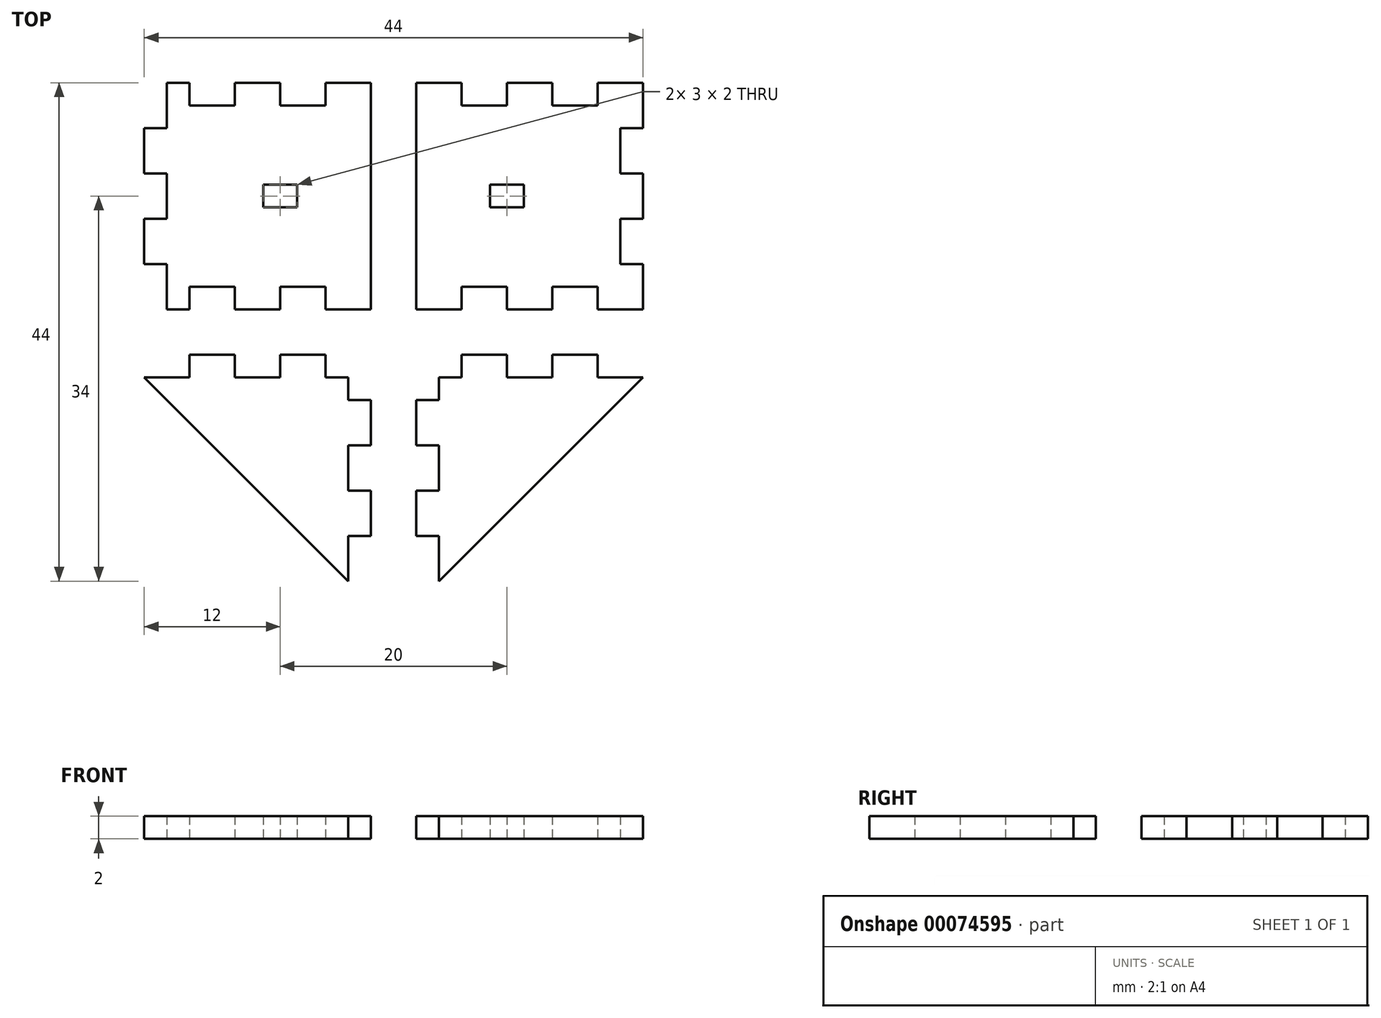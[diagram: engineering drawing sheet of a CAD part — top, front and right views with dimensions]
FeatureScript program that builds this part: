
annotation { "Feature Type Name" : "Feature", "Feature Type Description" : "" }
export const myFeature = defineFeature(function(context is Context, id is Id, definition is map)
    precondition{}
    {
        {
            var Q0;
            Q0=qCreatedBy(makeId("Top.planeOp"),FACE);
            var sketch = newSketch(context, id + "F3", { "sketchPlane" : qUnion([Q0])});
            skLineSegment(sketch, "E0", {"start": v(2, 0) * mm, "end": v(6, 0) * mm});
            skLineSegment(sketch, "E1", {"start": v(6, 0) * mm, "end": v(6, 2) * mm});
            skLineSegment(sketch, "E2", {"start": v(6, 2) * mm, "end": v(10, 2) * mm});
            skLineSegment(sketch, "E3", {"start": v(10, 2) * mm, "end": v(10, 0) * mm});
            skLineSegment(sketch, "E4", {"start": v(10, 0) * mm, "end": v(14, 0) * mm});
            skLineSegment(sketch, "E5", {"start": v(14, 0) * mm, "end": v(14, 2) * mm});
            skLineSegment(sketch, "E6", {"start": v(14, 2) * mm, "end": v(18, 2) * mm});
            skLineSegment(sketch, "E7", {"start": v(18, 2) * mm, "end": v(18, 0) * mm});
            skLineSegment(sketch, "E8", {"start": v(18, 0) * mm, "end": v(22, 0) * mm});
            skLineSegment(sketch, "E9", {"start": v(22, 0) * mm, "end": v(22, 4) * mm});
            skLineSegment(sketch, "E10", {"start": v(22, 4) * mm, "end": v(20, 4) * mm});
            skLineSegment(sketch, "E11", {"start": v(20, 4) * mm, "end": v(20, 8) * mm});
            skLineSegment(sketch, "E12", {"start": v(20, 8) * mm, "end": v(22, 8) * mm});
            skLineSegment(sketch, "E13", {"start": v(22, 8) * mm, "end": v(22, 12) * mm});
            skLineSegment(sketch, "E14", {"start": v(22, 12) * mm, "end": v(20, 12) * mm});
            skLineSegment(sketch, "E15", {"start": v(20, 12) * mm, "end": v(20, 16) * mm});
            skLineSegment(sketch, "E16", {"start": v(20, 16) * mm, "end": v(22, 16) * mm});
            skLineSegment(sketch, "E17", {"start": v(22, 16) * mm, "end": v(22, 20) * mm});
            skLineSegment(sketch, "E18", {"start": v(22, 20) * mm, "end": v(18, 20) * mm});
            skLineSegment(sketch, "E19", {"start": v(18, 20) * mm, "end": v(18, 18) * mm});
            skLineSegment(sketch, "E20", {"start": v(18, 18) * mm, "end": v(14, 18) * mm});
            skLineSegment(sketch, "E21", {"start": v(14, 18) * mm, "end": v(14, 20) * mm});
            skLineSegment(sketch, "E22", {"start": v(14, 20) * mm, "end": v(10, 20) * mm});
            skLineSegment(sketch, "E23", {"start": v(10, 20) * mm, "end": v(10, 18) * mm});
            skLineSegment(sketch, "E24", {"start": v(10, 18) * mm, "end": v(6, 18) * mm});
            skLineSegment(sketch, "E25", {"start": v(6, 18) * mm, "end": v(6, 20) * mm});
            skLineSegment(sketch, "E26", {"start": v(6, 20) * mm, "end": v(2, 20) * mm});
            skLineSegment(sketch, "E27", {"start": v(2, 20) * mm, "end": v(2, 0) * mm});
            skLineSegment(sketch, "E28", {"start": v(-2, 0) * mm, "end": v(-2, 20) * mm});
            skLineSegment(sketch, "E29", {"start": v(-2, 20) * mm, "end": v(-6, 20) * mm});
            skLineSegment(sketch, "E30", {"start": v(-6, 20) * mm, "end": v(-6, 18) * mm});
            skLineSegment(sketch, "E31", {"start": v(-6, 18) * mm, "end": v(-10, 18) * mm});
            skLineSegment(sketch, "E32", {"start": v(-10, 18) * mm, "end": v(-10, 20) * mm});
            skLineSegment(sketch, "E33", {"start": v(-10, 20) * mm, "end": v(-14, 20) * mm});
            skLineSegment(sketch, "E34", {"start": v(-14, 20) * mm, "end": v(-14, 18) * mm});
            skLineSegment(sketch, "E35", {"start": v(-14, 18) * mm, "end": v(-18, 18) * mm});
            skLineSegment(sketch, "E36", {"start": v(-18, 18) * mm, "end": v(-18, 20) * mm});
            skLineSegment(sketch, "E37", {"start": v(-18, 20) * mm, "end": v(-20, 20) * mm});
            skLineSegment(sketch, "E38", {"start": v(-20, 20) * mm, "end": v(-20, 16) * mm});
            skLineSegment(sketch, "E39", {"start": v(-20, 16) * mm, "end": v(-22, 16) * mm});
            skLineSegment(sketch, "E40", {"start": v(-22, 16) * mm, "end": v(-22, 12) * mm});
            skLineSegment(sketch, "E41", {"start": v(-22, 12) * mm, "end": v(-20, 12) * mm});
            skLineSegment(sketch, "E42", {"start": v(-20, 12) * mm, "end": v(-20, 8) * mm});
            skLineSegment(sketch, "E43", {"start": v(-20, 8) * mm, "end": v(-22, 8) * mm});
            skLineSegment(sketch, "E44", {"start": v(-22, 8) * mm, "end": v(-22, 4) * mm});
            skLineSegment(sketch, "E45", {"start": v(-22, 4) * mm, "end": v(-20, 4) * mm});
            skLineSegment(sketch, "E46", {"start": v(-20, 4) * mm, "end": v(-20, 0) * mm});
            skLineSegment(sketch, "E47", {"start": v(-20, 0) * mm, "end": v(-18, 0) * mm});
            skLineSegment(sketch, "E48", {"start": v(-18, 0) * mm, "end": v(-18, 2) * mm});
            skLineSegment(sketch, "E49", {"start": v(-18, 2) * mm, "end": v(-14, 2) * mm});
            skLineSegment(sketch, "E50", {"start": v(-14, 2) * mm, "end": v(-14, 0) * mm});
            skLineSegment(sketch, "E51", {"start": v(-14, 0) * mm, "end": v(-10, 0) * mm});
            skLineSegment(sketch, "E52", {"start": v(-10, 0) * mm, "end": v(-10, 2) * mm});
            skLineSegment(sketch, "E53", {"start": v(-10, 2) * mm, "end": v(-6, 2) * mm});
            skLineSegment(sketch, "E54", {"start": v(-6, 2) * mm, "end": v(-6, 0) * mm});
            skLineSegment(sketch, "E55", {"start": v(-6, 0) * mm, "end": v(-2, 0) * mm});
            skLineSegment(sketch, "E56", {"start": v(-4, -6) * mm, "end": v(-6, -6) * mm});
            skLineSegment(sketch, "E57", {"start": v(-6, -6) * mm, "end": v(-6, -4) * mm});
            skLineSegment(sketch, "E58", {"start": v(-6, -4) * mm, "end": v(-10, -4) * mm});
            skLineSegment(sketch, "E59", {"start": v(-10, -4) * mm, "end": v(-10, -6) * mm});
            skLineSegment(sketch, "E60", {"start": v(-10, -6) * mm, "end": v(-14, -6) * mm});
            skLineSegment(sketch, "E61", {"start": v(-14, -6) * mm, "end": v(-14, -4) * mm});
            skLineSegment(sketch, "E62", {"start": v(-14, -4) * mm, "end": v(-18, -4) * mm});
            skLineSegment(sketch, "E63", {"start": v(-18, -4) * mm, "end": v(-18, -6) * mm});
            skLineSegment(sketch, "E64", {"start": v(-18, -6) * mm, "end": v(-22, -6) * mm});
            skLineSegment(sketch, "E65", {"start": v(-22, -6) * mm, "end": v(-4, -24) * mm});
            skLineSegment(sketch, "E66", {"start": v(-4, -24) * mm, "end": v(-4, -20) * mm});
            skLineSegment(sketch, "E67", {"start": v(-4, -20) * mm, "end": v(-2, -20) * mm});
            skLineSegment(sketch, "E68", {"start": v(-2, -20) * mm, "end": v(-2, -16) * mm});
            skLineSegment(sketch, "E69", {"start": v(-2, -16) * mm, "end": v(-4, -16) * mm});
            skLineSegment(sketch, "E70", {"start": v(-4, -16) * mm, "end": v(-4, -12) * mm});
            skLineSegment(sketch, "E71", {"start": v(-4, -12) * mm, "end": v(-2, -12) * mm});
            skLineSegment(sketch, "E72", {"start": v(-2, -12) * mm, "end": v(-2, -8) * mm});
            skLineSegment(sketch, "E73", {"start": v(-2, -8) * mm, "end": v(-4, -8) * mm});
            skLineSegment(sketch, "E74", {"start": v(-4, -8) * mm, "end": v(-4, -6) * mm});
            skLineSegment(sketch, "E75", {"start": v(4, -6) * mm, "end": v(6, -6) * mm});
            skLineSegment(sketch, "E76", {"start": v(6, -6) * mm, "end": v(6, -4) * mm});
            skLineSegment(sketch, "E77", {"start": v(6, -4) * mm, "end": v(10, -4) * mm});
            skLineSegment(sketch, "E78", {"start": v(10, -4) * mm, "end": v(10, -6) * mm});
            skLineSegment(sketch, "E79", {"start": v(10, -6) * mm, "end": v(14, -6) * mm});
            skLineSegment(sketch, "E80", {"start": v(14, -6) * mm, "end": v(14, -4) * mm});
            skLineSegment(sketch, "E81", {"start": v(14, -4) * mm, "end": v(18, -4) * mm});
            skLineSegment(sketch, "E82", {"start": v(18, -4) * mm, "end": v(18, -6) * mm});
            skLineSegment(sketch, "E83", {"start": v(18, -6) * mm, "end": v(22, -6) * mm});
            skLineSegment(sketch, "E84", {"start": v(22, -6) * mm, "end": v(4, -24) * mm});
            skLineSegment(sketch, "E85", {"start": v(4, -24) * mm, "end": v(4, -20) * mm});
            skLineSegment(sketch, "E86", {"start": v(4, -20) * mm, "end": v(2, -20) * mm});
            skLineSegment(sketch, "E87", {"start": v(2, -20) * mm, "end": v(2, -16) * mm});
            skLineSegment(sketch, "E88", {"start": v(2, -16) * mm, "end": v(4, -16) * mm});
            skLineSegment(sketch, "E89", {"start": v(4, -16) * mm, "end": v(4, -12) * mm});
            skLineSegment(sketch, "E90", {"start": v(4, -12) * mm, "end": v(2, -12) * mm});
            skLineSegment(sketch, "E91", {"start": v(2, -12) * mm, "end": v(2, -8) * mm});
            skLineSegment(sketch, "E92", {"start": v(2, -8) * mm, "end": v(4, -8) * mm});
            skLineSegment(sketch, "E93", {"start": v(4, -8) * mm, "end": v(4, -6) * mm});
            skSolve(sketch);
        }
        {
            var Q0;
            Q0=makeQuery(id+"F3.imprint","IMPRINT",FACE,{"disambiguationData":[TD([[makeQuery(id+"F3.imprint","IMPRINT",EDGE,{"derivedFrom":sQuery(id+"F3.wireOp",EDGE,"E28")}),1.0]])]});
            var Q1;
            Q1=makeQuery(id+"F3.imprint","IMPRINT",FACE,{"disambiguationData":[TD([[makeQuery(id+"F3.imprint","IMPRINT",EDGE,{"derivedFrom":sQuery(id+"F3.wireOp",EDGE,"E0")}),1.0]])]});
            var Q2;
            Q2=makeQuery(id+"F3.imprint","IMPRINT",FACE,{"disambiguationData":[TD([[makeQuery(id+"F3.imprint","IMPRINT",EDGE,{"derivedFrom":sQuery(id+"F3.wireOp",EDGE,"E56")}),1.0]])]});
            var Q3;
            Q3=makeQuery(id+"F3.imprint","IMPRINT",FACE,{"disambiguationData":[TD([[makeQuery(id+"F3.imprint","IMPRINT",EDGE,{"derivedFrom":sQuery(id+"F3.wireOp",EDGE,"E75")}),-1.0]])]});
            extrude(context, id + "F0", {"entities" : qUnion([Q0, Q1, Q2, Q3]), "depth" : 2 * mm});
        }
        {
            var Q0;
            Q0=qCreatedBy(makeId("Top.planeOp"),FACE);
            var sketch = newSketch(context, id + "F1", { "sketchPlane" : qUnion([Q0])});
            skLineSegment(sketch, "E94.bottom", {"start": v(8.5, 11) * mm, "end": v(11.5, 11) * mm});
            skLineSegment(sketch, "E94.top", {"start": v(8.5, 9) * mm, "end": v(11.5, 9) * mm});
            skLineSegment(sketch, "E94.left", {"start": v(8.5, 11) * mm, "end": v(8.5, 9) * mm});
            skLineSegment(sketch, "E94.right", {"start": v(11.5, 11) * mm, "end": v(11.5, 9) * mm});
            skLineSegment(sketch, "E95.bottom", {"start": v(-11.5, 11) * mm, "end": v(-8.5, 11) * mm});
            skLineSegment(sketch, "E95.top", {"start": v(-11.5, 9) * mm, "end": v(-8.5, 9) * mm});
            skLineSegment(sketch, "E95.left", {"start": v(-11.5, 11) * mm, "end": v(-11.5, 9) * mm});
            skLineSegment(sketch, "E95.right", {"start": v(-8.5, 11) * mm, "end": v(-8.5, 9) * mm});
            skSolve(sketch);
        }
        {
            var Q0;
            Q0=makeQuery(id+"F1.imprint","IMPRINT",FACE,{"disambiguationData":[TD([[makeQuery(id+"F1.imprint","IMPRINT",EDGE,{"derivedFrom":sQuery(id+"F1.wireOp",EDGE,"E94.bottom")}),-1.0]])]});
            extrude(context, id + "F4", {"entities" : qUnion([Q0]), "operationType" : NewBodyOperationType.REMOVE, "depth" : 2 * mm});
        }
        {
            var Q0;
            Q0=makeQuery(id+"F1.imprint","IMPRINT",FACE,{"disambiguationData":[TD([[makeQuery(id+"F1.imprint","IMPRINT",EDGE,{"derivedFrom":sQuery(id+"F1.wireOp",EDGE,"E95.bottom")}),-1.0]])]});
            extrude(context, id + "F2", {"entities" : qUnion([Q0]), "operationType" : NewBodyOperationType.REMOVE, "depth" : 25 * mm});
        }
    });
